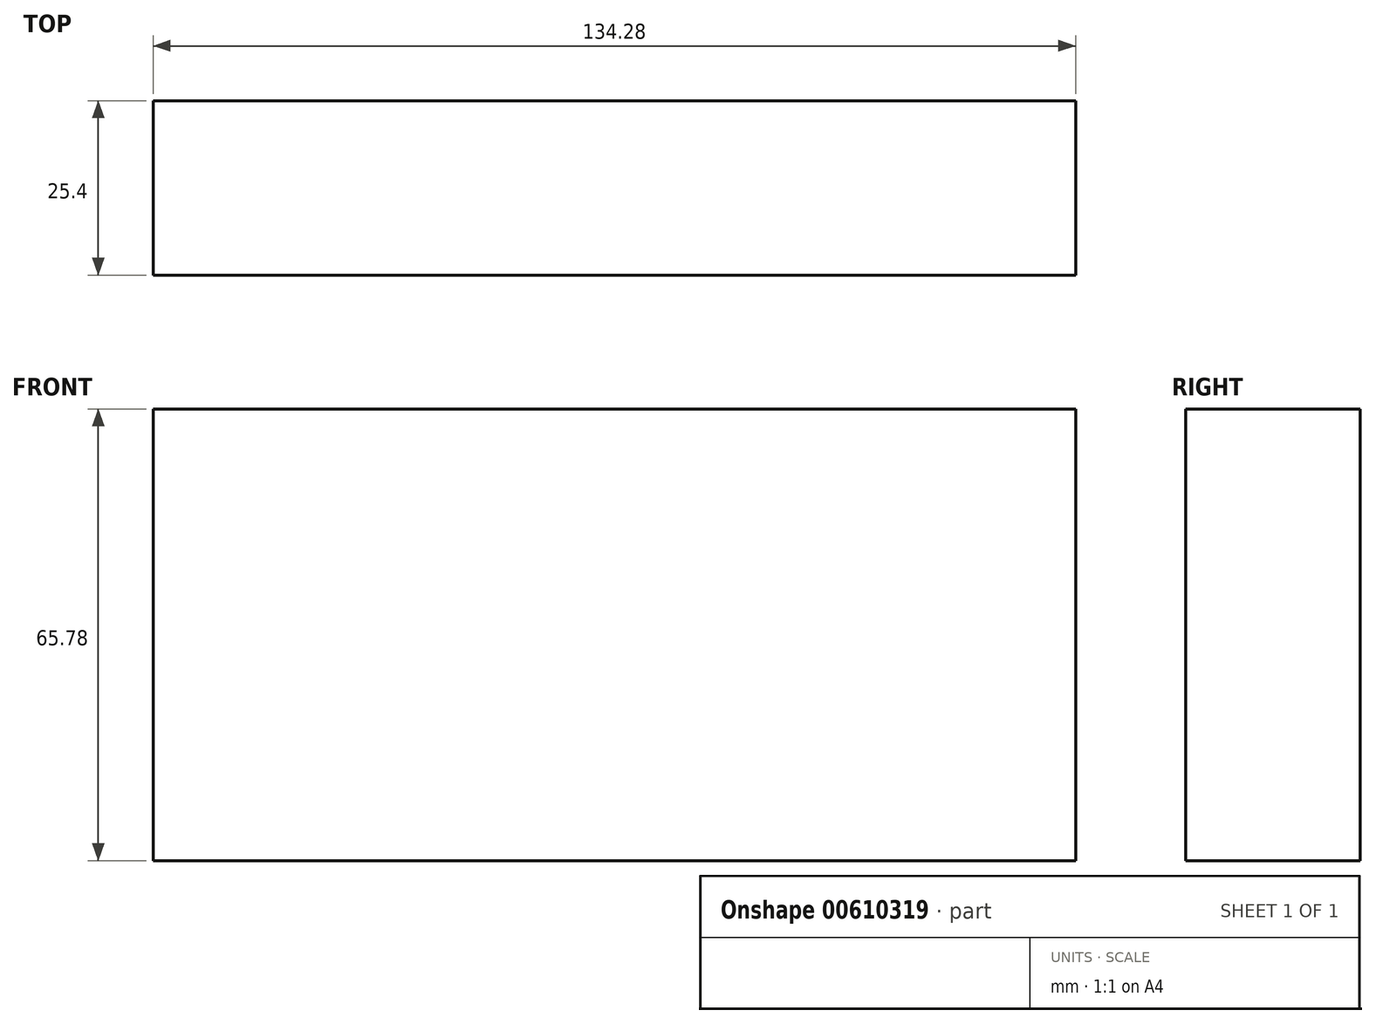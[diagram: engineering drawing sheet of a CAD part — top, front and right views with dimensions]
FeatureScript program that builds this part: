
annotation { "Feature Type Name" : "Feature", "Feature Type Description" : "" }
export const myFeature = defineFeature(function(context is Context, id is Id, definition is map)
    precondition{}
    {
        {
            var Q0;
            Q0=qCreatedBy(makeId("Front.planeOp"),FACE);
            var sketch = newSketch(context, id + "F0", { "sketchPlane" : qUnion([Q0])});
            skLineSegment(sketch, "E0.bottom", {"start": v(0, 0) * mm, "end": v(134.28, 0) * mm});
            skLineSegment(sketch, "E0.top", {"start": v(0, 65.78) * mm, "end": v(134.28, 65.78) * mm});
            skLineSegment(sketch, "E0.left", {"start": v(0, 0) * mm, "end": v(0, 65.78) * mm});
            skLineSegment(sketch, "E0.right", {"start": v(134.28, 0) * mm, "end": v(134.28, 65.78) * mm});
            skSolve(sketch);
        }
        {
            var Q0;
            Q0 = qSketchRegion(id + "F0", true);
            extrude(context, id + "F1", {"entities" : qUnion([Q0]), "depth" : 25.4 * mm, "offsetDistance" : 25.4 * mm});
        }
    });
